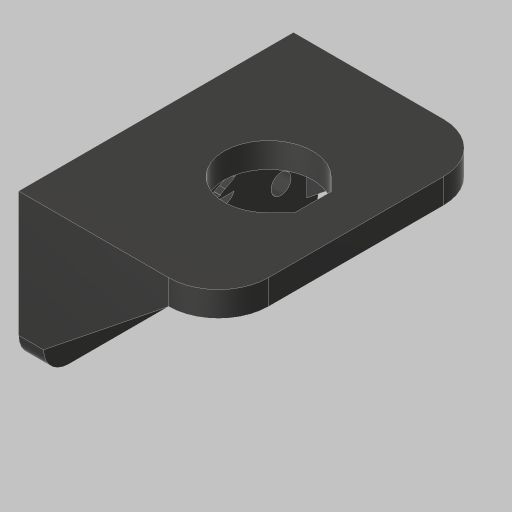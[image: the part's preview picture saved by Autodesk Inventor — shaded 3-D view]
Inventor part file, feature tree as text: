
AUTODESK INVENTOR PART (.ipt)
format: ipt  version: 2023.5 (Build 275446000, 446)  size: 379,392 bytes
history: native  units: in
note: dims shown in document units (in); Inventor stores cm internally (conversion verified against a paired STEP export)
features: sketch x5, extrude x4, fillet x4, projected_geometry x4, hole x1, mirror x1, chamfer x1
ambient origin geometry x8: Origin, YZ Plane, XZ Plane, XY Plane, X Axis, Y Axis, Z Axis, Center Point
bodies: Solid1 (feature_tree)
feature tree (20):
  extrude  "Extrusion1"  Depth=1.5in
  sketch  "Sketch2"  dims[d2=0.25in d3=0.25in]
  hole  "Hole1"  [1 undecoded]
  extrude  "Extrusion2"  Depth=0.886in
  fillet  "Fillet1"  Radius=2.0in
  fillet  "Fillet2"  Radius=0.5in
  fillet  "Fillet3"  Radius=0.126in
  extrude  "Extrusion3"  TaperAngle=0.0deg  [1 undecoded]
  mirror  "Mirror1"
  fillet  "Fillet4"  Radius=0.0315in
  extrude  "Extrusion4"  Depth=0.5in
  chamfer  "Chamfer1"  Distance=0.25in
  sketch  "Sketch1"  dims[d0=2.0in d1=1.5in]
  projected_geometry  "Projected Loop1"
  sketch  "Sketch3"  dims[d4=2.75in d5=0.0in d6=0.886in d7=2.0in d8=0.5in]
  projected_geometry  "Projected Loop2"
  projected_geometry  "Projected Loop3"
  sketch  "Sketch5"  dims[d9=0.201in d10=0.236in d11=0.385in d12=0.25in d13=0.5635in d14=1.0in d15=0.8108in d16=0.126in]
  projected_geometry  "Projected Loop4"
  sketch  "Sketch6"  dims[d17=0.5098in d18=0.0in d19=0.0in d20=0.0315in d21=0.5in d22=0.25in d23=0.1181in d24=0.0in d25=0.125in d26=0.125in d27=45.0deg d28=0.25in d29=0.3in d30=1.1743in d31=0.0in d32=0.0in]
note: 2 required parameter values undecoded (feature->parameter linkage not recoverable at this tier; creation-order binding heuristic only, values carry confidence <= 0.55)
